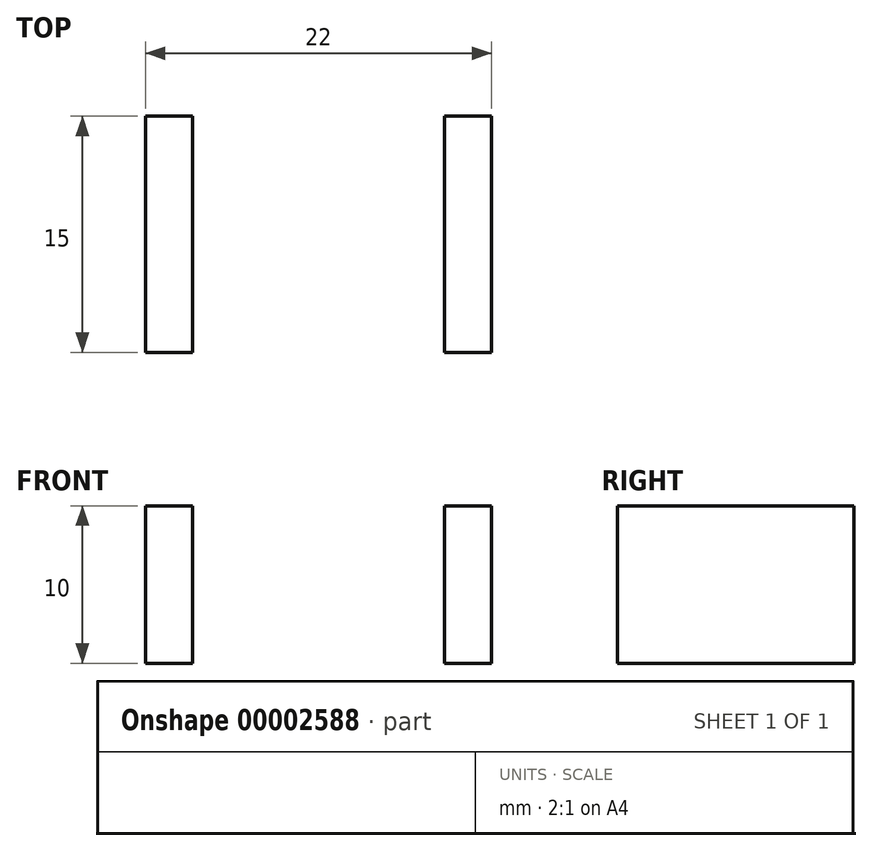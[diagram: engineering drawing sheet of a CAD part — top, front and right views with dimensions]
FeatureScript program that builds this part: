
annotation { "Feature Type Name" : "Feature", "Feature Type Description" : "" }
export const myFeature = defineFeature(function(context is Context, id is Id, definition is map)
    precondition{}
    {
        {
            var Q0;
            Q0=qCreatedBy(makeId("Top.planeOp"),FACE);
            var sketch = newSketch(context, id + "F0", { "sketchPlane" : qUnion([Q0])});
            skLineSegment(sketch, "E0.bottom", {"start": v(-11, 7.5) * mm, "end": v(-8, 7.5) * mm});
            skLineSegment(sketch, "E0.top", {"start": v(-11, -7.5) * mm, "end": v(-8, -7.5) * mm});
            skLineSegment(sketch, "E0.left", {"start": v(-11, 7.5) * mm, "end": v(-11, -7.5) * mm});
            skLineSegment(sketch, "E0.right", {"start": v(-8, 7.5) * mm, "end": v(-8, -7.5) * mm});
            skPoint(sketch, "E1", {"position": v(-8, 0) * mm});
            skLineSegment(sketch, "E2", {"start": v(-8, 0) * mm, "end": v(0, 0) * mm, "construction": true});
            skLineSegment(sketch, "E3", {"start": v(0, 0) * mm, "end": v(0, -7.48) * mm, "construction": true});
            skLineSegment(sketch, "E4.MirrorCS", {"start": v(11, 7.5) * mm, "end": v(8, 7.5) * mm});
            skLineSegment(sketch, "E5.MirrorCS", {"start": v(11, -7.5) * mm, "end": v(8, -7.5) * mm});
            skLineSegment(sketch, "E6.MirrorCS", {"start": v(8, 7.5) * mm, "end": v(8, -7.5) * mm});
            skLineSegment(sketch, "E7.MirrorCS", {"start": v(11, 7.5) * mm, "end": v(11, -7.5) * mm});
            skFitSpline(sketch, "E8", {"points": [v(-8, 4.58) * mm, v(-3.91, 5.58) * mm, v(0, 7.54) * mm], "startDerivative": vector(21.7, -17.92) * mm, "endDerivative": vector(9.8, 0.37) * mm});
            skFitSpline(sketch, "E9.MirrorCS", {"points": [v(8, 4.58) * mm, v(3.91, 5.58) * mm, v(0, 7.54) * mm], "startDerivative": vector(-21.7, -17.92) * mm, "endDerivative": vector(-9.8, 0.37) * mm});
            skFitSpline(sketch, "E10.MirrorCS", {"points": [v(-8, -4.58) * mm, v(-3.91, -5.58) * mm, v(0, -7.54) * mm], "startDerivative": vector(21.7, 17.92) * mm, "endDerivative": vector(9.8, -0.37) * mm});
            skSolve(sketch);
        }
        {
            var Q0;
            Q0 = qSketchRegion(id + "F0", true);
            extrude(context, id + "F1", {"entities" : qUnion([Q0]), "depth" : 10 * mm});
        }
    });
